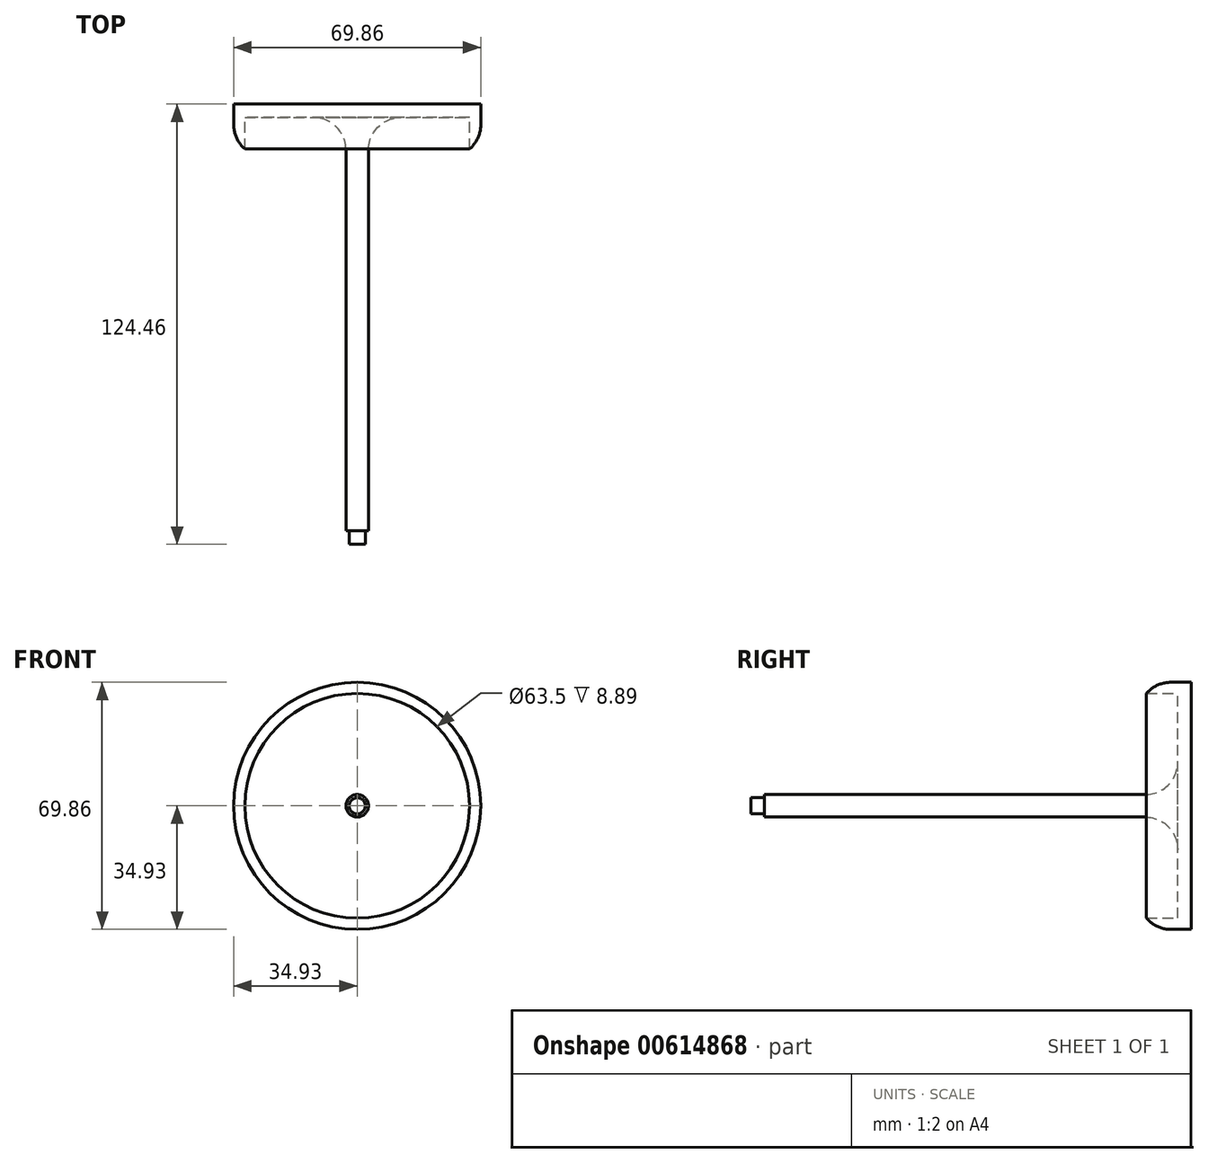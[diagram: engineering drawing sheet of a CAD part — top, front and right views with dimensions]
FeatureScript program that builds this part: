
annotation { "Feature Type Name" : "Feature", "Feature Type Description" : "" }
export const myFeature = defineFeature(function(context is Context, id is Id, definition is map)
    precondition{}
    {
        {
            var Q0;
            Q0=qCreatedBy(makeId("Front.planeOp"),FACE);
            var sketch = newSketch(context, id + "F0", { "sketchPlane" : qUnion([Q0])});
            skCircle(sketch, "E0", {"center": v(0, 0) * mm, "radius": 31.75 * mm});
            skCircle(sketch, "E1", {"center": v(0, 0) * mm, "radius": 3.18 * mm});
            skCircle(sketch, "E2", {"center": v(0, 0) * mm, "radius": 34.93 * mm});
            skSolve(sketch);
        }
        {
            var Q0;
            Q0=makeQuery(id+"F0.imprint","IMPRINT",FACE,{"disambiguationData":[TD([[makeQuery(id+"F0.imprint","IMPRINT",EDGE,{"derivedFrom":sQuery(id+"F0.wireOp",EDGE,"E0")}),1.0]])]});
            var Q1;
            Q1=makeQuery(id+"F0.imprint","IMPRINT",FACE,{"disambiguationData":[TD([[makeQuery(id+"F0.imprint","IMPRINT",EDGE,{"derivedFrom":sQuery(id+"F0.wireOp",EDGE,"E1")}),1.0]])]});
            extrude(context, id + "F1", {"entities" : qUnion([Q0, Q1]), "depth" : 3.8 * mm, "offsetDistance" : 25.4 * mm});
        }
        {
            var Q0;
            Q0=makeQuery(id+"F0.imprint","IMPRINT",FACE,{"disambiguationData":[TD([[makeQuery(id+"F0.imprint","IMPRINT",EDGE,{"derivedFrom":sQuery(id+"F0.wireOp",EDGE,"E1")}),1.0]])]});
            var Q1;
            Q1=sQuery(id+"F0.wireOp",EDGE,"E1");
            extrude(context, id + "F2", {"entities" : qUnion([Q0]), "operationType" : NewBodyOperationType.ADD, "surfaceEntities" : qUnion([Q1]), "depth" : 124.46 * mm, "offsetDistance" : 25.4 * mm});
        }
        {
            var Q0;
            Q0=makeQuery(id+"F0.imprint","IMPRINT",FACE,{"disambiguationData":[TD([[makeQuery(id+"F0.imprint","IMPRINT",EDGE,{"derivedFrom":sQuery(id+"F0.wireOp",EDGE,"E0")}),-1.0]])]});
            extrude(context, id + "F3", {"entities" : qUnion([Q0]), "operationType" : NewBodyOperationType.ADD, "depth" : 12.7 * mm, "offsetDistance" : 25.4 * mm});
        }
        {
            var Q0;
            Q0=makeQuery(id+"F3.opExtrude","CAP_EDGE",EDGE,{"disambiguationData":[OSD([sQuery(id+"F0.wireOp",EDGE,"E2")])],"isStart":false});
            var Q1;
            Q1=makeQuery(id+"F1.opExtrude","CAP_EDGE",EDGE,{"disambiguationData":[OSD([sQuery(id+"F0.wireOp",EDGE,"E0")])],"isStart":false});
            var Q2;
            Q2=makeQuery(id+"F2.boolean.opBoolean","INTERSECT",EDGE,{"derivedFrom":[makeQuery(id+"F1.opExtrude","CAP_FACE",FACE,{"disambiguationData":[OSD([sQuery(id+"F0.wireOp",EDGE,"E0")])],"isStart":false}),makeQuery(id+"F2.opExtrude","SWEPT_FACE",FACE,{"disambiguationData":[OSD([sQuery(id+"F0.wireOp",EDGE,"E1")])]})]});
            fillet(context, id + "F4", {"entities" : qUnion([Q0, Q1, Q2]), "radius" : 9.2 * mm, "tangentPropagation" : true, "allowEdgeOverflow" : false});
        }
        {
            var Q0;
            Q0=makeQuery(id+"F2.opExtrude","CAP_FACE",FACE,{"disambiguationData":[OSD([sQuery(id+"F0.wireOp",EDGE,"E1")])],"isStart":false});
            var sketch = newSketch(context, id + "F5", { "sketchPlane" : qUnion([Q0])});
            skCircle(sketch, "E3", {"center": v(0, 0) * mm, "radius": 2.29 * mm});
            skSolve(sketch);
        }
        {
            var Q0;
            Q0=makeQuery(id+"F5.imprint","IMPRINT",FACE,{"disambiguationData":[TD([[makeQuery(id+"F5.imprint","IMPRINT",EDGE,{"derivedFrom":sQuery(id+"F5.wireOp",EDGE,"E3")}),-1.0]])]});
            extrude(context, id + "F6", {"entities" : qUnion([Q0]), "operationType" : NewBodyOperationType.REMOVE, "oppositeDirection" : true, "depth" : 3.8 * mm, "offsetDistance" : 25.4 * mm});
        }
    });
